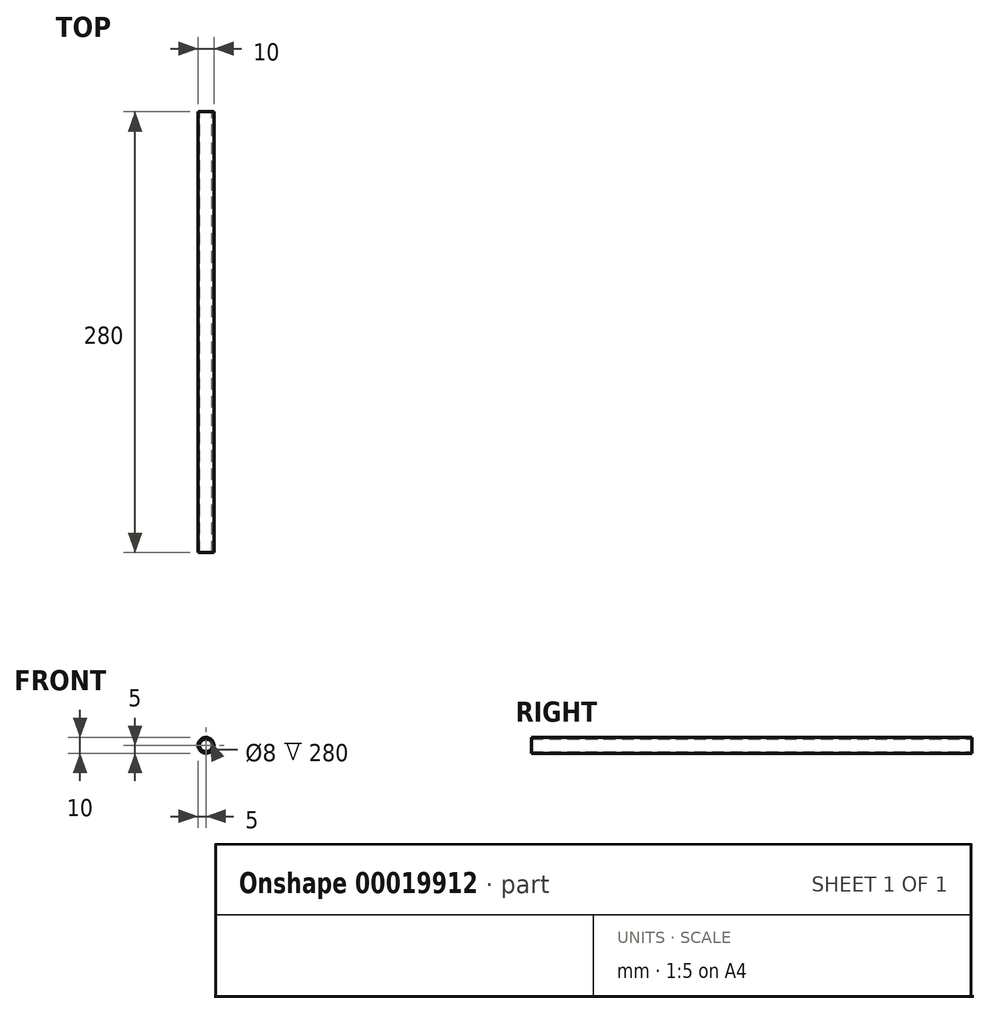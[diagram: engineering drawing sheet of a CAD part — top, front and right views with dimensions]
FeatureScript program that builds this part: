
annotation { "Feature Type Name" : "Feature", "Feature Type Description" : "" }
export const myFeature = defineFeature(function(context is Context, id is Id, definition is map)
    precondition{}
    {
        {
            var Q0;
            Q0=qCreatedBy(makeId("Front.planeOp"),FACE);
            var sketch = newSketch(context, id + "F0", { "sketchPlane" : qUnion([Q0])});
            skCircle(sketch, "E0", {"center": v(0, 0) * mm, "radius": 4 * mm});
            skCircle(sketch, "E1", {"center": v(0, 0) * mm, "radius": 5 * mm});
            skSolve(sketch);
        }
        {
            var Q0;
            Q0 = qSketchRegion(id + "F0", true);
            extrude(context, id + "F1", {"entities" : qUnion([Q0]), "depth" : 280 * mm});
        }
    });
